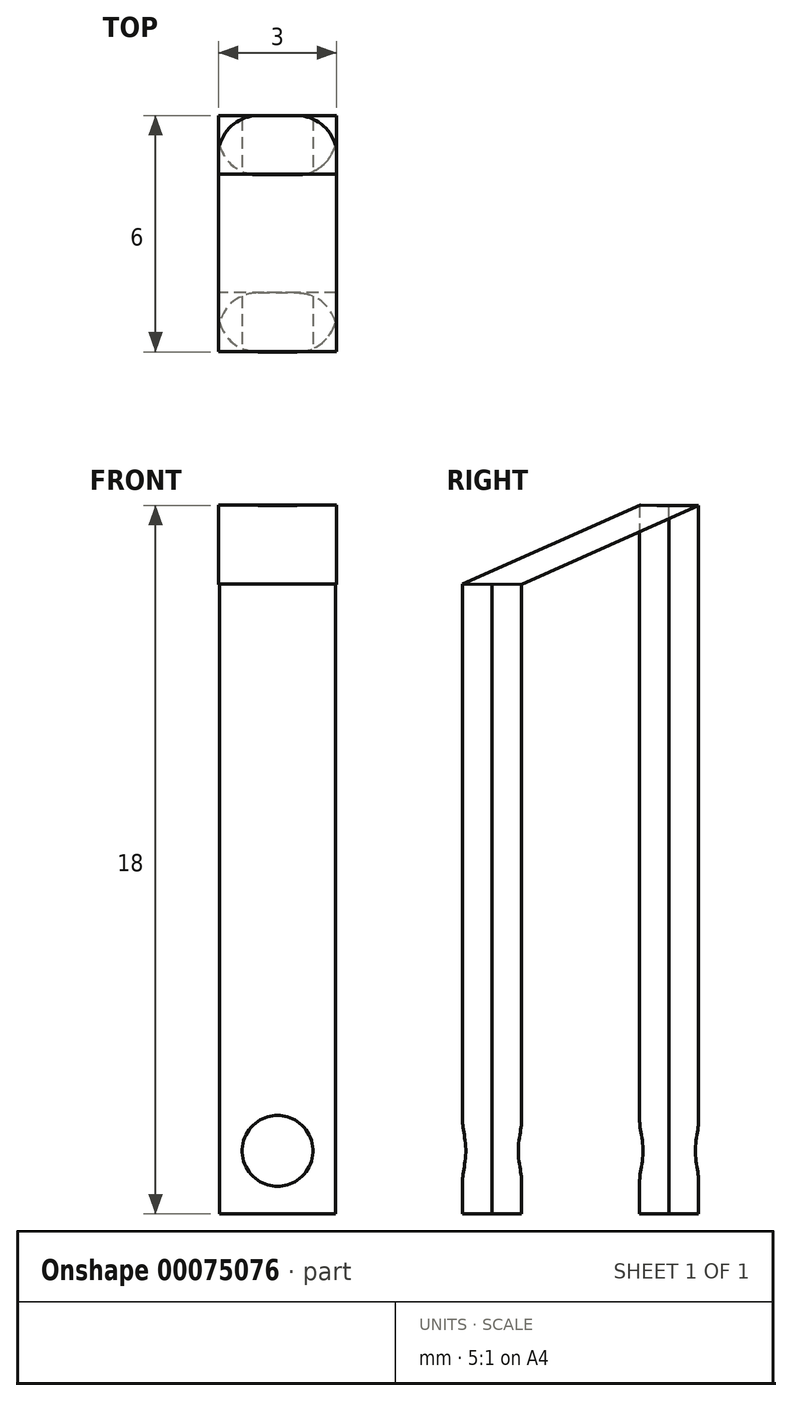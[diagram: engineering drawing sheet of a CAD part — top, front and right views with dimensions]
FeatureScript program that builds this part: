
annotation { "Feature Type Name" : "Feature", "Feature Type Description" : "" }
export const myFeature = defineFeature(function(context is Context, id is Id, definition is map)
    precondition{}
    {
        {
            var Q0;
            Q0=qCreatedBy(makeId("Front.planeOp"),FACE);
            var sketch = newSketch(context, id + "F0", { "sketchPlane" : qUnion([Q0])});
            skLineSegment(sketch, "E0.bottom", {"start": v(-1.5, 9) * mm, "end": v(1.5, 9) * mm});
            skLineSegment(sketch, "E0.top", {"start": v(-1.5, -9) * mm, "end": v(1.5, -9) * mm});
            skLineSegment(sketch, "E0.left", {"start": v(-1.5, 9) * mm, "end": v(-1.5, -9) * mm});
            skLineSegment(sketch, "E0.right", {"start": v(1.5, 9) * mm, "end": v(1.5, -9) * mm});
            skPoint(sketch, "E0.middle", {"position": v(0, 0) * mm});
            skSolve(sketch);
        }
        {
            var Q0;
            Q0=makeQuery(id+"F0.imprint","IMPRINT",FACE,{"disambiguationData":[TD([[makeQuery(id+"F0.imprint","IMPRINT",EDGE,{"derivedFrom":sQuery(id+"F0.wireOp",EDGE,"E0.bottom")}),-1.0]])]});
            extrude(context, id + "F1", {"entities" : qUnion([Q0]), "depth" : 1.5 * mm});
        }
        {
            var Q0;
            Q0=qCreatedBy(makeId("Front.planeOp"),FACE);
            cPlane(context, id + "F2", {"entities" : qUnion([Q0]), "cplaneType" : CPlaneType.OFFSET, "offset" : 4.5 * mm, "width" : 150 * mm, "height" : 150 * mm});
        }
        {
            var Q0;
            Q0=qCreatedBy(id+"F2.planeOp",FACE);
            var sketch = newSketch(context, id + "F3", { "sketchPlane" : qUnion([Q0])});
            skLineSegment(sketch, "E1.bottom", {"start": v(1.5, -9) * mm, "end": v(-1.5, -9) * mm});
            skLineSegment(sketch, "E1.top", {"start": v(1.5, 7) * mm, "end": v(-1.5, 7) * mm});
            skLineSegment(sketch, "E1.left", {"start": v(1.5, -9) * mm, "end": v(1.5, 7) * mm});
            skLineSegment(sketch, "E1.right", {"start": v(-1.5, -9) * mm, "end": v(-1.5, 7) * mm});
            skSolve(sketch);
        }
        {
            var Q0;
            Q0=makeQuery(id+"F3.imprint","IMPRINT",FACE,{"disambiguationData":[TD([[makeQuery(id+"F3.imprint","IMPRINT",EDGE,{"derivedFrom":sQuery(id+"F3.wireOp",EDGE,"E1.bottom")}),-1.0]])]});
            extrude(context, id + "F4", {"entities" : qUnion([Q0]), "depth" : 1.5 * mm});
        }
        {
            var Q0;
            Q0=makeQuery(id+"F4.opExtrude","CAP_FACE",FACE,{"disambiguationData":[OSD([sQuery(id+"F3.wireOp",EDGE,"E1.bottom"),sQuery(id+"F3.wireOp",EDGE,"E1.top"),sQuery(id+"F3.wireOp",EDGE,"E1.left"),sQuery(id+"F3.wireOp",EDGE,"E1.right")])],"isStart":false});
            var sketch = newSketch(context, id + "F5", { "sketchPlane" : qUnion([Q0])});
            skCircle(sketch, "E2", {"center": v(0, -7.4) * mm, "radius": 0.9 * mm});
            skSolve(sketch);
        }
        {
            var Q0;
            Q0=makeQuery(id+"F5.imprint","IMPRINT",FACE,{"disambiguationData":[TD([[makeQuery(id+"F5.imprint","IMPRINT",EDGE,{"derivedFrom":sQuery(id+"F5.wireOp",EDGE,"E2")}),1.0]])]});
            extrude(context, id + "F6", {"entities" : qUnion([Q0]), "operationType" : NewBodyOperationType.REMOVE, "endBound" : BoundingType.THROUGH_ALL, "oppositeDirection" : true, "depth" : 25 * mm});
        }
        {
            var Q0;
            Q0=qCreatedBy(makeId("Right.planeOp"),FACE);
            var sketch = newSketch(context, id + "F7", { "sketchPlane" : qUnion([Q0])});
            skLineSegment(sketch, "E3", {"start": v(-1.48, 9) * mm, "end": v(-6, 7) * mm});
            skLineSegment(sketch, "E4", {"start": v(0, 9) * mm, "end": v(-4.5, 7) * mm});
            skLineSegment(sketch, "E5", {"start": v(-4.5, 7) * mm, "end": v(-6, 7) * mm});
            skLineSegment(sketch, "E6", {"start": v(0, 9) * mm, "end": v(-1.48, 9) * mm});
            skSolve(sketch);
        }
        {
            var Q0;
            Q0=makeQuery(id+"F7.imprint","IMPRINT",FACE,{"disambiguationData":[TD([[makeQuery(id+"F7.imprint","IMPRINT",EDGE,{"derivedFrom":sQuery(id+"F7.wireOp",EDGE,"E3")}),1.0]])]});
            extrude(context, id + "F8", {"entities" : qUnion([Q0]), "endBound" : BoundingType.SYMMETRIC, "depth" : 3 * mm});
        }
        {
            var Q0;
            Q0=makeQuery(id+"F1.opExtrude","CAP_EDGE",EDGE,{"disambiguationData":[OSD([sQuery(id+"F0.wireOp",EDGE,"E0.left")])],"isStart":true});
            var Q1;
            Q1=makeQuery(id+"F1.opExtrude","CAP_EDGE",EDGE,{"disambiguationData":[OSD([sQuery(id+"F0.wireOp",EDGE,"E0.right")])],"isStart":true});
            var Q2;
            Q2=makeQuery(id+"F1.opExtrude","CAP_EDGE",EDGE,{"disambiguationData":[OSD([sQuery(id+"F0.wireOp",EDGE,"E0.left")])],"isStart":false});
            var Q3;
            Q3=makeQuery(id+"F1.opExtrude","CAP_EDGE",EDGE,{"disambiguationData":[OSD([sQuery(id+"F0.wireOp",EDGE,"E0.right")])],"isStart":false});
            var Q4;
            Q4=makeQuery(id+"F4.opExtrude","CAP_EDGE",EDGE,{"disambiguationData":[OSD([sQuery(id+"F3.wireOp",EDGE,"E1.left")])],"isStart":true});
            var Q5;
            Q5=makeQuery(id+"F4.opExtrude","CAP_EDGE",EDGE,{"disambiguationData":[OSD([sQuery(id+"F3.wireOp",EDGE,"E1.right")])],"isStart":true});
            var Q6;
            Q6=makeQuery(id+"F4.opExtrude","CAP_EDGE",EDGE,{"disambiguationData":[OSD([sQuery(id+"F3.wireOp",EDGE,"E1.left")])],"isStart":false});
            var Q7;
            Q7=makeQuery(id+"F4.opExtrude","CAP_EDGE",EDGE,{"disambiguationData":[OSD([sQuery(id+"F3.wireOp",EDGE,"E1.right")])],"isStart":false});
            fillet(context, id + "F9", {"entities" : qUnion([Q0, Q1, Q2, Q3, Q4, Q5, Q6, Q7]), "radius" : 1 * mm, "tangentPropagation" : true, "allowEdgeOverflow" : false});
        }
    });
